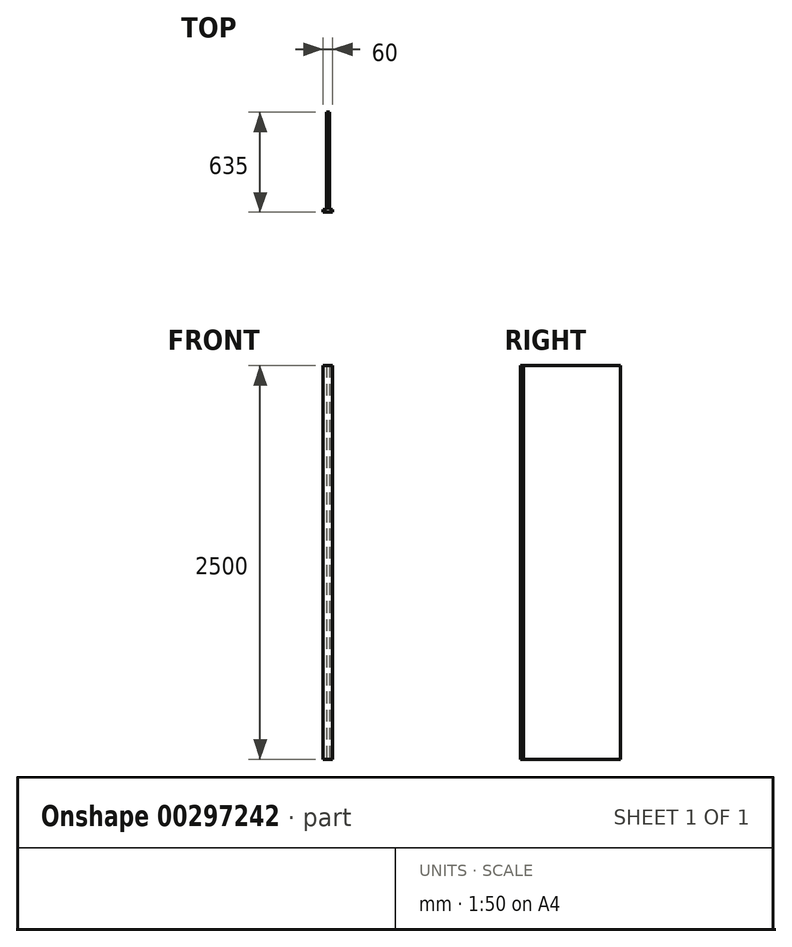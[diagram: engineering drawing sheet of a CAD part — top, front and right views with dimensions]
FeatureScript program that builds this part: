
annotation { "Feature Type Name" : "Feature", "Feature Type Description" : "" }
export const myFeature = defineFeature(function(context is Context, id is Id, definition is map)
    precondition{}
    {
        {
            var Q0;
            Q0=qCreatedBy(makeId("Right.planeOp"),FACE);
            var sketch = newSketch(context, id + "F0", { "sketchPlane" : qUnion([Q0])});
            skLineSegment(sketch, "E0.bottom", {"start": v(317.5, 1250) * mm, "end": v(-317.5, 1250) * mm});
            skLineSegment(sketch, "E0.top", {"start": v(317.5, -1250) * mm, "end": v(-317.5, -1250) * mm});
            skLineSegment(sketch, "E0.left", {"start": v(317.5, 1250) * mm, "end": v(317.5, -1250) * mm});
            skLineSegment(sketch, "E0.right", {"start": v(-317.5, 1250) * mm, "end": v(-317.5, -1250) * mm});
            skPoint(sketch, "E0.middle", {"position": v(0, 0) * mm});
            skSolve(sketch);
        }
        {
            var Q0;
            Q0=makeQuery(id+"F0.imprint","IMPRINT",FACE,{"disambiguationData":[TD([[makeQuery(id+"F0.imprint","IMPRINT",EDGE,{"derivedFrom":sQuery(id+"F0.wireOp",EDGE,"E0.bottom")}),1.0]])]});
            extrude(context, id + "F1", {"entities" : qUnion([Q0]), "depth" : 18 * mm});
        }
        {
            var Q0;
            Q0=makeQuery(id+"F1.opExtrude","SWEPT_FACE",FACE,{"disambiguationData":[OSD([sQuery(id+"F0.wireOp",EDGE,"E0.bottom")])]});
            var sketch = newSketch(context, id + "F2", { "sketchPlane" : qUnion([Q0])});
            skLineSegment(sketch, "E1.bottom", {"start": v(39, -317.5) * mm, "end": v(-21, -317.5) * mm});
            skLineSegment(sketch, "E1.top", {"start": v(39, -299.5) * mm, "end": v(-21, -299.5) * mm});
            skLineSegment(sketch, "E1.left", {"start": v(39, -317.5) * mm, "end": v(39, -299.5) * mm});
            skLineSegment(sketch, "E1.right", {"start": v(-21, -317.5) * mm, "end": v(-21, -299.5) * mm});
            skSolve(sketch);
        }
        {
            var Q0;
            Q0 = qSketchRegion(id + "F2", true);
            extrude(context, id + "F3", {"entities" : qUnion([Q0]), "operationType" : NewBodyOperationType.ADD, "oppositeDirection" : true, "depth" : 2500 * mm});
        }
    });
